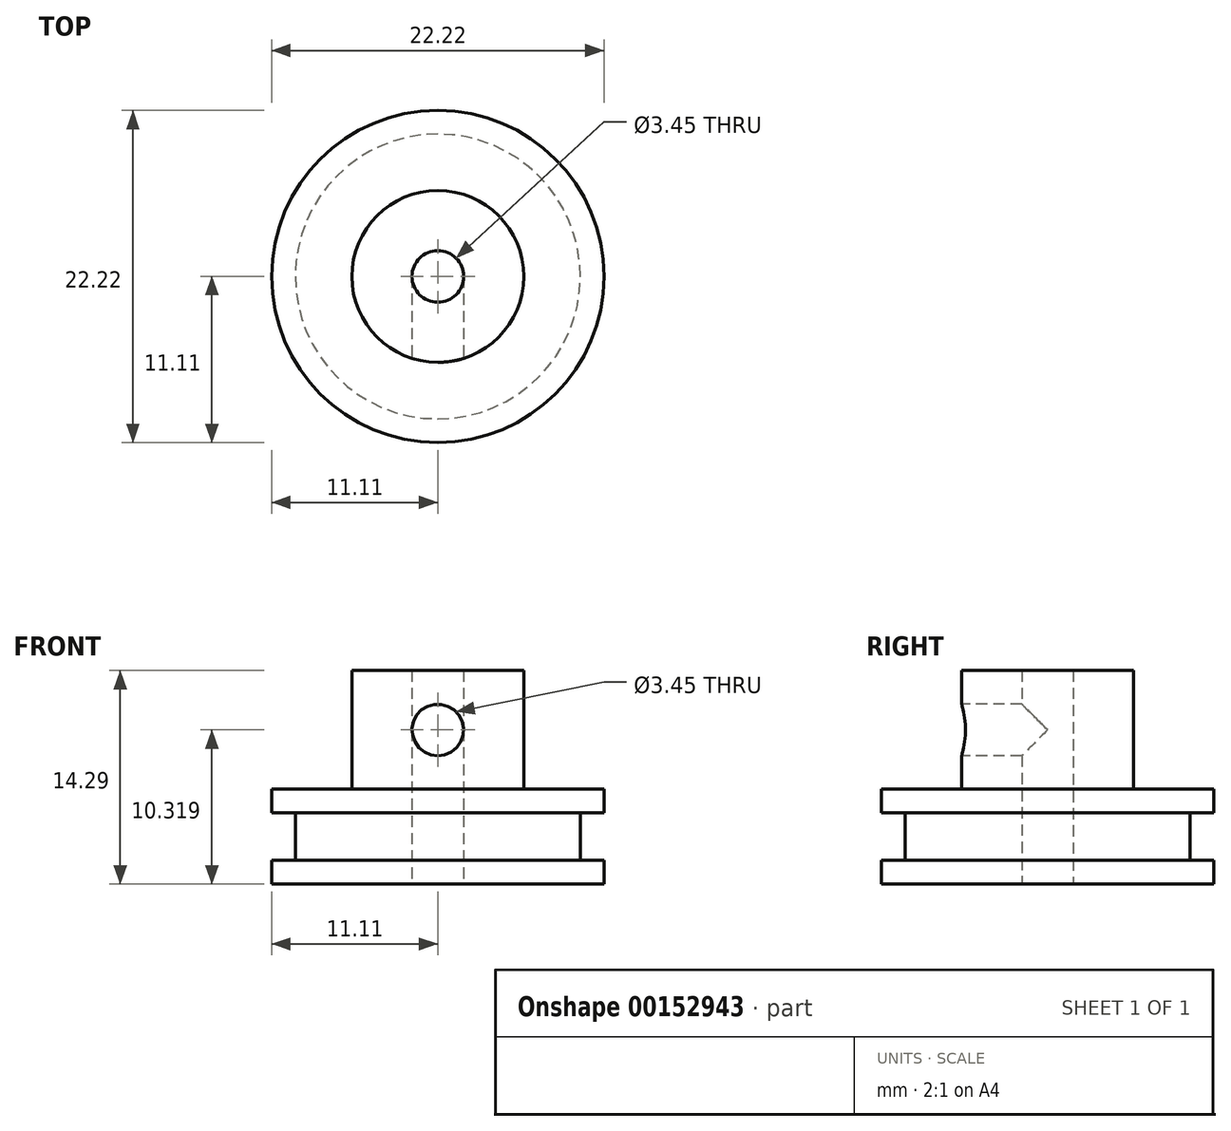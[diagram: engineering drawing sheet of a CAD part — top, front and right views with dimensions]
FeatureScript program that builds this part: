
annotation { "Feature Type Name" : "Feature", "Feature Type Description" : "" }
export const myFeature = defineFeature(function(context is Context, id is Id, definition is map)
    precondition{}
    {
        {
            var Q0;
            Q0=qCreatedBy(makeId("Top.planeOp"),FACE);
            var sketch = newSketch(context, id + "F0", { "sketchPlane" : qUnion([Q0])});
            skLineSegment(sketch, "E0.bottom", {"start": v(12.7, -12.7) * mm, "end": v(-12.7, -12.7) * mm});
            skLineSegment(sketch, "E0.top", {"start": v(12.7, 12.7) * mm, "end": v(-12.7, 12.7) * mm});
            skLineSegment(sketch, "E0.left", {"start": v(12.7, -12.7) * mm, "end": v(12.7, 12.7) * mm});
            skLineSegment(sketch, "E0.right", {"start": v(-12.7, -12.7) * mm, "end": v(-12.7, 12.7) * mm});
            skPoint(sketch, "E0.middle", {"position": v(0, 0) * mm});
            skCircle(sketch, "E1", {"center": v(0, 0) * mm, "radius": 12.7 * mm, "construction": true});
            skCircle(sketch, "E2", {"center": v(0, 0) * mm, "radius": 1.73 * mm});
            skCircle(sketch, "E3", {"center": v(0, 0) * mm, "radius": 2.15 * mm, "construction": true});
            skLineSegment(sketch, "E4.bottom", {"start": v(-2.15, -12.52) * mm, "end": v(2.15, -12.52) * mm, "construction": true});
            skLineSegment(sketch, "E4.top", {"start": v(-2.15, -2.15) * mm, "end": v(2.15, -2.15) * mm, "construction": true});
            skLineSegment(sketch, "E4.left", {"start": v(-2.15, -12.52) * mm, "end": v(-2.15, -2.15) * mm, "construction": true});
            skLineSegment(sketch, "E4.right", {"start": v(2.15, -12.52) * mm, "end": v(2.15, -2.15) * mm, "construction": true});
            skSolve(sketch);
        }
        {
            var Q0;
            Q0 = qSketchRegion(id + "F0", true);
            extrude(context, id + "F1", {"entities" : qUnion([Q0]), "depth" : 7.94 * mm});
        }
        {
            var Q0;
            Q0=makeQuery(id+"F1.opExtrude","SWEPT_FACE",FACE,{"disambiguationData":[OSD([sQuery(id+"F0.wireOp",EDGE,"E0.bottom")])]});
            var sketch = newSketch(context, id + "F2", { "sketchPlane" : qUnion([Q0])});
            skLineSegment(sketch, "E5", {"start": v(0, 7.94) * mm, "end": v(0, 0) * mm, "construction": true});
            skCircle(sketch, "E6", {"center": v(0, 3.97) * mm, "radius": 1.73 * mm});
            skSolve(sketch);
        }
        {
            var Q0;
            Q0 = qSketchRegion(id + "F2", true);
            var Q1;
            Q1=makeQuery(id+"F1.opExtrude","SWEPT_FACE",FACE,{"disambiguationData":[OSD([sQuery(id+"F0.wireOp",EDGE,"E2")])]});
            extrude(context, id + "F3", {"entities" : qUnion([Q0]), "operationType" : NewBodyOperationType.REMOVE, "endBound" : BoundingType.UP_TO_SURFACE, "oppositeDirection" : true, "endBoundEntityFace" : qUnion([Q1]), "depth" : 25.4 * mm});
        }
        {
            var Q0;
            Q0=makeQuery(id+"F1.opExtrude","CAP_FACE",FACE,{"disambiguationData":[OSD([sQuery(id+"F0.wireOp",EDGE,"E0.bottom"),sQuery(id+"F0.wireOp",EDGE,"E0.top"),sQuery(id+"F0.wireOp",EDGE,"E0.left"),sQuery(id+"F0.wireOp",EDGE,"E0.right"),sQuery(id+"F0.wireOp",EDGE,"E2")])],"isStart":false});
            var sketch = newSketch(context, id + "F4", { "sketchPlane" : qUnion([Q0])});
            skCircle(sketch, "E7", {"center": v(0, 0) * mm, "radius": 5.75 * mm});
            skLineSegment(sketch, "E8.bottom", {"start": v(-12.7, -12.7) * mm, "end": v(12.7, -12.7) * mm});
            skLineSegment(sketch, "E8.top", {"start": v(-12.7, 12.7) * mm, "end": v(12.7, 12.7) * mm});
            skLineSegment(sketch, "E8.left", {"start": v(-12.7, -12.7) * mm, "end": v(-12.7, 12.7) * mm});
            skLineSegment(sketch, "E8.right", {"start": v(12.7, -12.7) * mm, "end": v(12.7, 12.7) * mm});
            skSolve(sketch);
        }
        {
            var Q0;
            Q0 = qSketchRegion(id + "F4", true);
            var Q1;
            Q1=makeQuery(id+"F1.opExtrude","CAP_FACE",FACE,{"disambiguationData":[OSD([sQuery(id+"F0.wireOp",EDGE,"E0.bottom"),sQuery(id+"F0.wireOp",EDGE,"E0.top"),sQuery(id+"F0.wireOp",EDGE,"E0.left"),sQuery(id+"F0.wireOp",EDGE,"E0.right"),sQuery(id+"F0.wireOp",EDGE,"E2")])],"isStart":true});
            extrude(context, id + "F5", {"entities" : qUnion([Q0]), "operationType" : NewBodyOperationType.REMOVE, "endBound" : BoundingType.UP_TO_SURFACE, "oppositeDirection" : true, "endBoundEntityFace" : qUnion([Q1]), "depth" : 25.4 * mm});
        }
        {
            var Q0;
            Q0=makeQuery(id+"F1.opExtrude","CAP_FACE",FACE,{"disambiguationData":[OSD([sQuery(id+"F0.wireOp",EDGE,"E0.bottom"),sQuery(id+"F0.wireOp",EDGE,"E0.top"),sQuery(id+"F0.wireOp",EDGE,"E0.left"),sQuery(id+"F0.wireOp",EDGE,"E0.right"),sQuery(id+"F0.wireOp",EDGE,"E2")])],"isStart":true});
            var sketch = newSketch(context, id + "F6", { "sketchPlane" : qUnion([Q0])});
            skCircle(sketch, "E9", {"center": v(0, 0) * mm, "radius": 11.11 * mm});
            skCircle(sketch, "E10", {"center": v(0, 0) * mm, "radius": 1.73 * mm});
            skSolve(sketch);
        }
        {
            var Q0;
            Q0 = qSketchRegion(id + "F6", true);
            extrude(context, id + "F7", {"entities" : qUnion([Q0]), "operationType" : NewBodyOperationType.ADD, "depth" : 1.59 * mm});
        }
        {
            var Q0;
            Q0=makeQuery(id+"F7.opExtrude","CAP_FACE",FACE,{"disambiguationData":[OSD([sQuery(id+"F6.wireOp",EDGE,"E9"),sQuery(id+"F6.wireOp",EDGE,"E10")])],"isStart":false});
            var sketch = newSketch(context, id + "F8", { "sketchPlane" : qUnion([Q0])});
            skCircle(sketch, "E11", {"center": v(0, 0) * mm, "radius": 9.53 * mm});
            skCircle(sketch, "E12", {"center": v(0, 0) * mm, "radius": 1.73 * mm});
            skSolve(sketch);
        }
        {
            var Q0;
            Q0 = qSketchRegion(id + "F8", true);
            extrude(context, id + "F9", {"entities" : qUnion([Q0]), "operationType" : NewBodyOperationType.ADD, "depth" : 3.17 * mm});
        }
        {
            var Q0;
            Q0=makeQuery(id+"F9.opExtrude","CAP_FACE",FACE,{"disambiguationData":[OSD([sQuery(id+"F8.wireOp",EDGE,"E11"),sQuery(id+"F8.wireOp",EDGE,"E12")])],"isStart":false});
            var sketch = newSketch(context, id + "F10", { "sketchPlane" : qUnion([Q0])});
            skCircle(sketch, "E13", {"center": v(0, 0) * mm, "radius": 1.73 * mm});
            skCircle(sketch, "E14", {"center": v(0, 0) * mm, "radius": 11.11 * mm});
            skSolve(sketch);
        }
        {
            var Q0;
            Q0 = qSketchRegion(id + "F10", true);
            extrude(context, id + "F11", {"entities" : qUnion([Q0]), "operationType" : NewBodyOperationType.ADD, "depth" : 1.59 * mm});
        }
    });
